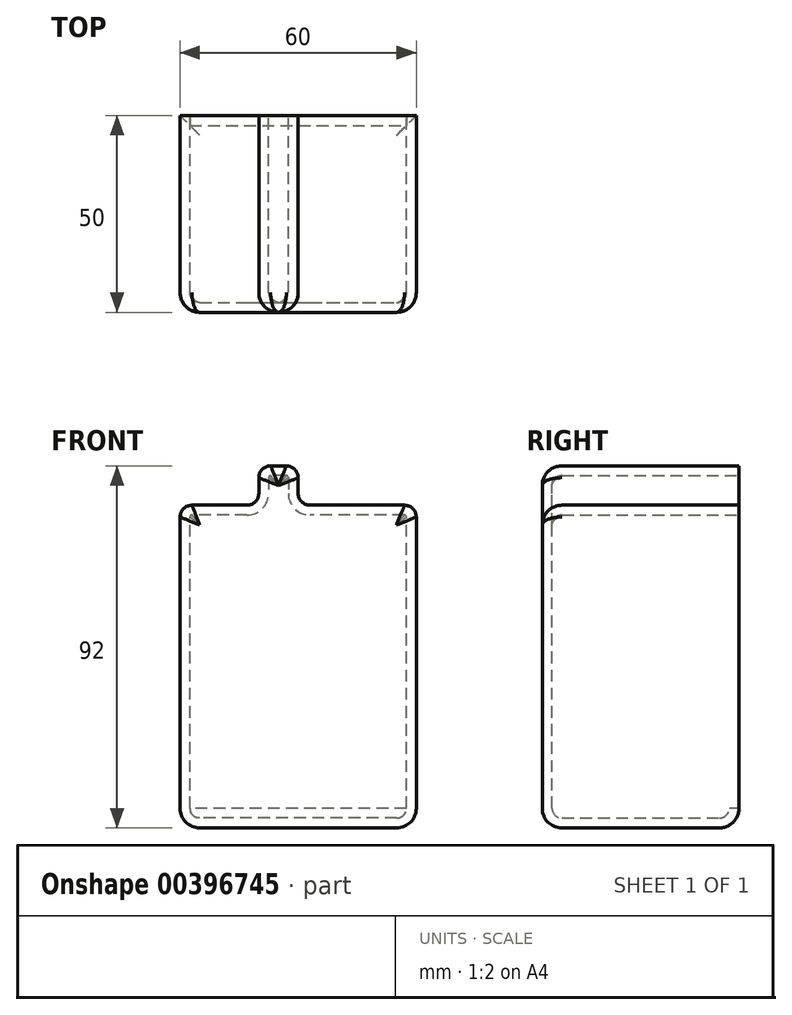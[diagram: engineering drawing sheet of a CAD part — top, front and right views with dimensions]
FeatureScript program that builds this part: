
annotation { "Feature Type Name" : "Feature", "Feature Type Description" : "" }
export const myFeature = defineFeature(function(context is Context, id is Id, definition is map)
    precondition{}
    {
        {
            var Q0;
            Q0=qCreatedBy(makeId("Front.planeOp"),FACE);
            var sketch = newSketch(context, id + "F0", { "sketchPlane" : qUnion([Q0])});
            skLineSegment(sketch, "E0.bottom", {"start": v(30, -41) * mm, "end": v(-30, -41) * mm});
            skLineSegment(sketch, "E0.top", {"start": v(30, 41) * mm, "end": v(0, 41) * mm});
            skLineSegment(sketch, "E0.left", {"start": v(30, -41) * mm, "end": v(30, 41) * mm});
            skLineSegment(sketch, "E0.right", {"start": v(-30, -41) * mm, "end": v(-30, 41) * mm});
            skPoint(sketch, "E0.middle", {"position": v(0, 0) * mm});
            skLineSegment(sketch, "E1.bottom", {"start": v(0, 51) * mm, "end": v(-10, 51) * mm});
            skLineSegment(sketch, "E1.left", {"start": v(0, 51) * mm, "end": v(0, 41) * mm});
            skLineSegment(sketch, "E1.right", {"start": v(-10, 51) * mm, "end": v(-10, 41) * mm});
            skPoint(sketch, "E1.middle", {"position": v(-5, 41) * mm});
            skPoint(sketch, "E2.orphan", {"position": v(-10, 31) * mm});
            skPoint(sketch, "E3.orphan", {"position": v(0, 31) * mm});
            skLineSegment(sketch, "E4.trimOffspring", {"start": v(-10, 41) * mm, "end": v(-30, 41) * mm});
            skSolve(sketch);
        }
        {
            var Q0;
            Q0 = qSketchRegion(id + "F0", true);
            extrude(context, id + "F1", {"entities" : qUnion([Q0]), "depth" : 50 * mm});
        }
        {
            var Q0;
            Q0=makeQuery(id+"F1.opExtrude","SWEPT_EDGE",EDGE,{"disambiguationData":[OSD([sQuery(id+"F0.wireOp",EDGE,"E0.top"),sQuery(id+"F0.wireOp",EDGE,"E1.left")])]});
            var Q1;
            Q1=makeQuery(id+"F1.opExtrude","SWEPT_EDGE",EDGE,{"disambiguationData":[OSD([sQuery(id+"F0.wireOp",EDGE,"E1.right"),sQuery(id+"F0.wireOp",EDGE,"E4.trimOffspring")])]});
            var Q2;
            Q2=makeQuery(id+"F1.opExtrude","SWEPT_EDGE",EDGE,{"disambiguationData":[OSD([sQuery(id+"F0.wireOp",EDGE,"E1.bottom"),sQuery(id+"F0.wireOp",EDGE,"E1.right")])]});
            var Q3;
            Q3=makeQuery(id+"F1.opExtrude","SWEPT_EDGE",EDGE,{"disambiguationData":[OSD([sQuery(id+"F0.wireOp",EDGE,"E1.bottom"),sQuery(id+"F0.wireOp",EDGE,"E1.left")])]});
            var Q4;
            Q4=makeQuery(id+"F1.opExtrude","SWEPT_EDGE",EDGE,{"disambiguationData":[OSD([sQuery(id+"F0.wireOp",EDGE,"E0.top"),sQuery(id+"F0.wireOp",EDGE,"E0.left")])]});
            var Q5;
            Q5=makeQuery(id+"F1.opExtrude","SWEPT_EDGE",EDGE,{"disambiguationData":[OSD([sQuery(id+"F0.wireOp",EDGE,"E0.right"),sQuery(id+"F0.wireOp",EDGE,"E4.trimOffspring")])]});
            fillet(context, id + "F2", {"entities" : qUnion([Q0, Q1, Q2, Q3, Q4, Q5]), "radius" : 3 * mm, "tangentPropagation" : true, "allowEdgeOverflow" : false});
        }
        {
            var Q0;
            Q0=makeQuery(id+"F1.opExtrude","CAP_EDGE",EDGE,{"disambiguationData":[OSD([sQuery(id+"F0.wireOp",EDGE,"E0.top")])],"isStart":false});
            fillet(context, id + "F3", {"entities" : qUnion([Q0]), "radius" : 5 * mm, "tangentPropagation" : true, "allowEdgeOverflow" : false});
        }
        {
            var Q0;
            Q0=makeQuery(id+"F1.opExtrude","SWEPT_FACE",FACE,{"disambiguationData":[OSD([sQuery(id+"F0.wireOp",EDGE,"E0.bottom")])]});
            fillet(context, id + "F4", {"entities" : qUnion([Q0]), "radius" : 5 * mm, "tangentPropagation" : true, "allowEdgeOverflow" : false});
        }
        {
            var Q0;
            Q0=makeQuery(id+"F1.opExtrude","CAP_FACE",FACE,{"disambiguationData":[OSD([sQuery(id+"F0.wireOp",EDGE,"E0.bottom"),sQuery(id+"F0.wireOp",EDGE,"E0.top"),sQuery(id+"F0.wireOp",EDGE,"E0.left"),sQuery(id+"F0.wireOp",EDGE,"E0.right"),sQuery(id+"F0.wireOp",EDGE,"E1.bottom"),sQuery(id+"F0.wireOp",EDGE,"E1.left"),sQuery(id+"F0.wireOp",EDGE,"E1.right"),sQuery(id+"F0.wireOp",EDGE,"E4.trimOffspring")])],"isStart":true});
            shell(context, id + "F5", {"entities" : qUnion([Q0]), "thickness" : 2.5 * mm});
        }
    });
